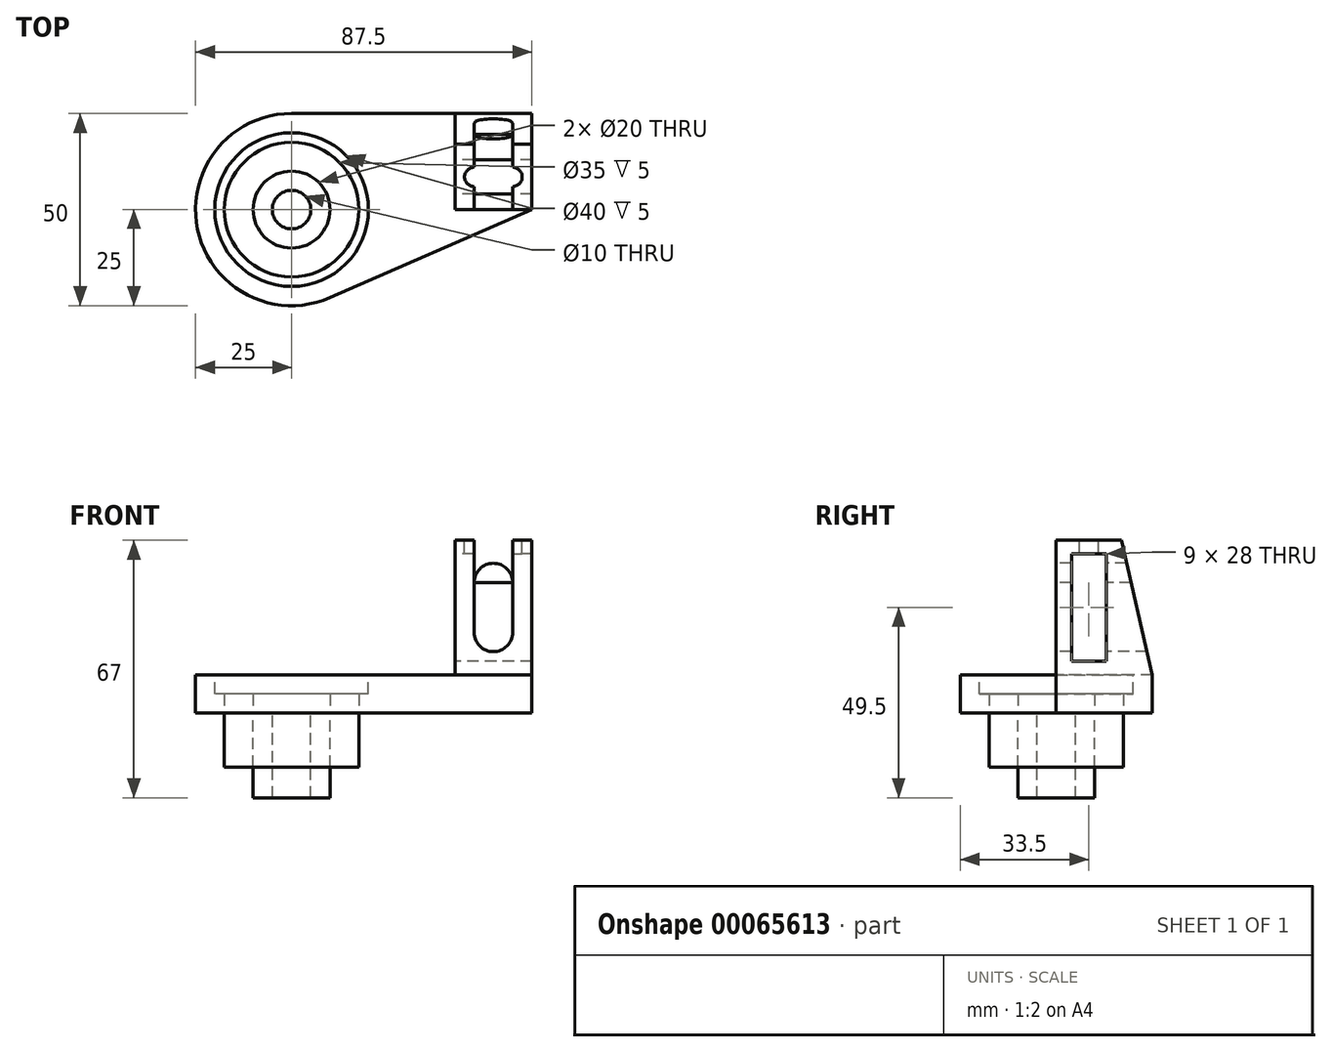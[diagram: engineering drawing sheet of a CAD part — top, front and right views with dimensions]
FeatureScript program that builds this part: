
annotation { "Feature Type Name" : "Feature", "Feature Type Description" : "" }
export const myFeature = defineFeature(function(context is Context, id is Id, definition is map)
    precondition{}
    {
        {
            var Q0;
            Q0=qCreatedBy(makeId("Top.planeOp"),FACE);
            var sketch = newSketch(context, id + "F0", { "sketchPlane" : qUnion([Q0])});
            skCircle(sketch, "E0", {"center": v(0, 0) * mm, "radius": 5 * mm});
            skCircle(sketch, "E1", {"center": v(0, 0) * mm, "radius": 10 * mm});
            skCircle(sketch, "E2", {"center": v(0, 0) * mm, "radius": 17.5 * mm});
            skCircle(sketch, "E3", {"center": v(0, 0) * mm, "radius": 20 * mm});
            skArc(sketch, "E4", {"start": v(0, 25) * mm, "mid": v(-24.47, -5.1) * mm, "end": v(10, -22.91) * mm});
            skLineSegment(sketch, "E5", {"start": v(0, 25) * mm, "end": v(42.5, 25) * mm});
            skLineSegment(sketch, "E6", {"start": v(10, -22.91) * mm, "end": v(62.5, 0) * mm});
            skLineSegment(sketch, "E7", {"start": v(62.5, 0) * mm, "end": v(62.5, 25) * mm});
            skLineSegment(sketch, "E8", {"start": v(62.5, 25) * mm, "end": v(42.5, 25) * mm});
            skLineSegment(sketch, "E9", {"start": v(42.5, 25) * mm, "end": v(42.5, 0) * mm});
            skLineSegment(sketch, "E10", {"start": v(42.5, 0) * mm, "end": v(62.5, 0) * mm});
            skLineSegment(sketch, "E11", {"start": v(62.5, 0) * mm, "end": v(62.5, 17) * mm});
            skLineSegment(sketch, "E12", {"start": v(62.5, 17) * mm, "end": v(42.5, 17) * mm});
            skSolve(sketch);
        }
        {
            var Q0;
            Q0=makeQuery(id+"F0.imprint","IMPRINT",FACE,{"disambiguationData":[TD([[makeQuery(id+"F0.imprint","IMPRINT",EDGE,{"derivedFrom":sQuery(id+"F0.wireOp",EDGE,"E3")}),-1.0]])]});
            var Q1;
            Q1=makeQuery(id+"F0.imprint","IMPRINT",FACE,{"disambiguationData":[TD([[makeQuery(id+"F0.imprint","IMPRINT",EDGE,{"derivedFrom":sQuery(id+"F0.wireOp",EDGE,"E2")}),-1.0]])]});
            extrude(context, id + "F1", {"entities" : qUnion([Q0, Q1]), "depth" : 10 * mm});
        }
        {
            var Q0;
            Q0=makeQuery(id+"F0.imprint","IMPRINT",FACE,{"disambiguationData":[TD([[makeQuery(id+"F0.imprint","IMPRINT",EDGE,{"derivedFrom":sQuery(id+"F0.wireOp",EDGE,"E7")}),1.0]])]});
            var Q1;
            {var subQ0=sQuery(id+"F0.wireOp",EDGE,"E10");Q1=makeQuery(id+"F0.imprint","IMPRINT",FACE,{"disambiguationData":[TD([[makeQuery(id+"F0.imprint","IMPRINT",EDGE,{"derivedFrom":subQ0}),1.0]])]});}
            extrude(context, id + "F2", {"entities" : qUnion([Q0, Q1]), "operationType" : NewBodyOperationType.ADD, "depth" : 45 * mm});
        }
        {
            var Q0;
            Q0=makeQuery(id+"F0.imprint","IMPRINT",FACE,{"disambiguationData":[TD([[makeQuery(id+"F0.imprint","IMPRINT",EDGE,{"derivedFrom":sQuery(id+"F0.wireOp",EDGE,"E0")}),-1.0]])]});
            extrude(context, id + "F3", {"entities" : qUnion([Q0]), "oppositeDirection" : true, "depth" : 22 * mm});
        }
        {
            var Q0;
            Q0=makeQuery(id+"F2.opExtrude","CAP_FACE",FACE,{"disambiguationData":[OSD([sQuery(id+"F0.wireOp",EDGE,"E7"),sQuery(id+"F0.wireOp",EDGE,"E8"),sQuery(id+"F0.wireOp",EDGE,"E9"),sQuery(id+"F0.wireOp",EDGE,"E10"),sQuery(id+"F0.wireOp",EDGE,"E11")])],"isStart":false});
            var sketch = newSketch(context, id + "F4", { "sketchPlane" : qUnion([Q0])});
            skLineSegment(sketch, "E13", {"start": v(62.5, 0) * mm, "end": v(62.5, 17) * mm});
            skLineSegment(sketch, "E14", {"start": v(62.5, 17) * mm, "end": v(42.5, 17) * mm});
            skLineSegment(sketch, "E15", {"start": v(62.5, 0) * mm, "end": v(57.5, 0) * mm});
            skLineSegment(sketch, "E16", {"start": v(57.5, 0) * mm, "end": v(47.5, 0) * mm});
            skLineSegment(sketch, "E17", {"start": v(47.5, 0) * mm, "end": v(42.5, 0) * mm});
            skLineSegment(sketch, "E18", {"start": v(42.5, 0) * mm, "end": v(42.5, 8.5) * mm});
            skLineSegment(sketch, "E19", {"start": v(42.5, 8.5) * mm, "end": v(62.5, 8.5) * mm});
            skLineSegment(sketch, "E20", {"start": v(57.5, 0) * mm, "end": v(57.5, 8.5) * mm});
            skLineSegment(sketch, "E21", {"start": v(47.5, 0) * mm, "end": v(47.5, 8.5) * mm});
            skCircle(sketch, "E22", {"center": v(47.5, 8.5) * mm, "radius": 2.5 * mm});
            skCircle(sketch, "E23", {"center": v(57.5, 8.5) * mm, "radius": 2.5 * mm});
            skSolve(sketch);
        }
        {
            var Q0;
            Q0=makeQuery(id+"F2.opExtrude","CAP_EDGE",EDGE,{"disambiguationData":[OSD([sQuery(id+"F0.wireOp",EDGE,"E8")])],"isStart":false});
            chamfer(context, id + "F5", {"entities" : qUnion([Q0]), "chamferType" : ChamferType.TWO_OFFSETS, "width1" : 8 * mm, "oppositeDirection" : false, "width2" : 35 * mm, "tangentPropagation" : true});
        }
        {
            var Q0;
            Q0=makeQuery(id+"F2.opExtrude","SWEPT_FACE",FACE,{"disambiguationData":[OSD([sQuery(id+"F0.wireOp",EDGE,"E9")])]});
            var sketch = newSketch(context, id + "F6", { "sketchPlane" : qUnion([Q0])});
            skLineSegment(sketch, "E24", {"start": v(0, 10) * mm, "end": v(0, 13.5) * mm});
            skLineSegment(sketch, "E25", {"start": v(0, 45) * mm, "end": v(-4, 45) * mm});
            skLineSegment(sketch, "E26", {"start": v(-4, 45) * mm, "end": v(-13, 45) * mm});
            skLineSegment(sketch, "E27", {"start": v(-13, 45) * mm, "end": v(-17, 45) * mm});
            skLineSegment(sketch, "E28", {"start": v(0, 45) * mm, "end": v(0, 41.5) * mm});
            skLineSegment(sketch, "E29", {"start": v(0, 41.5) * mm, "end": v(-17.8, 41.5) * mm});
            skLineSegment(sketch, "E30", {"start": v(-4, 45) * mm, "end": v(-4, 10) * mm});
            skLineSegment(sketch, "E31", {"start": v(0, 13.5) * mm, "end": v(-24.2, 13.5) * mm});
            skLineSegment(sketch, "E32", {"start": v(-13, 45) * mm, "end": v(-13, 10) * mm});
            skPoint(sketch, "E33", {"position": v(-13, 41.5) * mm});
            skPoint(sketch, "E34", {"position": v(-4, 41.5) * mm});
            skPoint(sketch, "E35", {"position": v(-4, 13.5) * mm});
            skPoint(sketch, "E36", {"position": v(-13, 13.5) * mm});
            skSolve(sketch);
        }
        {
            var Q0;
            {var subQ0=sQuery(id+"F6.wireOp",EDGE,"E30");var subQ1=sQuery(id+"F6.wireOp",EDGE,"E29");var subQ2=makeQuery(id+"F6.imprint","INTERSECT",VERTEX,{"derivedFrom":[subQ1,subQ0]});Q0=makeQuery(id+"F6.imprint","IMPRINT",FACE,{"disambiguationData":[TD([[makeQuery(id+"F6.imprint","IMPRINT",EDGE,{"disambiguationData":[TD([[subQ2,-1.0]])],"derivedFrom":subQ1}),1.0]])]});}
            extrude(context, id + "F7", {"entities" : qUnion([Q0]), "operationType" : NewBodyOperationType.REMOVE, "oppositeDirection" : true, "depth" : 30 * mm});
        }
        {
            var Q0;
            Q0=makeQuery(id+"F2.opExtrude","SWEPT_FACE",FACE,{"disambiguationData":[OSD([sQuery(id+"F0.wireOp",EDGE,"E10")])]});
            var sketch = newSketch(context, id + "F8", { "sketchPlane" : qUnion([Q0])});
            skLineSegment(sketch, "E37", {"start": v(62.5, 45) * mm, "end": v(62.5, 34) * mm});
            skLineSegment(sketch, "E38", {"start": v(62.5, 34) * mm, "end": v(62.5, 21) * mm});
            skLineSegment(sketch, "E39", {"start": v(42.5, 45) * mm, "end": v(47.5, 45) * mm});
            skLineSegment(sketch, "E40", {"start": v(47.5, 45) * mm, "end": v(57.5, 45) * mm});
            skLineSegment(sketch, "E41", {"start": v(57.5, 45) * mm, "end": v(62.5, 45) * mm});
            skLineSegment(sketch, "E42", {"start": v(57.5, 45) * mm, "end": v(57.5, 10) * mm});
            skLineSegment(sketch, "E43", {"start": v(47.5, 45) * mm, "end": v(47.5, 10) * mm});
            skLineSegment(sketch, "E44", {"start": v(62.5, 21) * mm, "end": v(42.5, 21) * mm});
            skLineSegment(sketch, "E45", {"start": v(62.5, 34) * mm, "end": v(42.5, 34) * mm});
            skArc(sketch, "E46", {"start": v(47.5, 34) * mm, "mid": v(52.5, 39) * mm, "end": v(57.5, 34) * mm});
            skArc(sketch, "E47", {"start": v(47.5, 21) * mm, "mid": v(52.5, 16) * mm, "end": v(57.5, 21) * mm});
            skPoint(sketch, "E47.startSnap0", {"position": v(52.5, 21) * mm});
            skSolve(sketch);
        }
        {
            var Q0;
            {var subQ0=sQuery(id+"F8.wireOp",EDGE,"E46");Q0=makeQuery(id+"F8.imprint","IMPRINT",FACE,{"disambiguationData":[TD([[makeQuery(id+"F8.imprint","IMPRINT",EDGE,{"derivedFrom":subQ0}),-1.0]])]});}
            var Q1;
            {var subQ0=sQuery(id+"F8.wireOp",EDGE,"E46");var subQ1=sQuery(id+"F8.wireOp",EDGE,"E45");var subQ2=sQuery(id+"F8.wireOp",EDGE,"E42");var subQ3=makeQuery(id+"F8.imprint","INTERSECT",VERTEX,{"derivedFrom":[subQ2,subQ1,subQ0]});Q1=makeQuery(id+"F8.imprint","IMPRINT",FACE,{"disambiguationData":[TD([[makeQuery(id+"F8.imprint","IMPRINT",EDGE,{"disambiguationData":[TD([[subQ3,-1.0]])],"derivedFrom":subQ2}),-1.0]])]});}
            var Q2;
            {var subQ0=sQuery(id+"F8.wireOp",EDGE,"E47");Q2=makeQuery(id+"F8.imprint","IMPRINT",FACE,{"disambiguationData":[TD([[makeQuery(id+"F8.imprint","IMPRINT",EDGE,{"derivedFrom":subQ0}),1.0]])]});}
            extrude(context, id + "F9", {"entities" : qUnion([Q0, Q1, Q2]), "operationType" : NewBodyOperationType.REMOVE, "oppositeDirection" : true, "depth" : 26 * mm});
        }
        {
            var Q0;
            {var subQ0=sQuery(id+"F4.wireOp",EDGE,"E19");var subQ1=makeQuery(id+"F4.imprint","INTERSECT",VERTEX,{"derivedFrom":[subQ0,sQuery(id+"F4.wireOp",EDGE,"E21")]});Q0=makeQuery(id+"F4.imprint","IMPRINT",FACE,{"disambiguationData":[TD([[makeQuery(id+"F4.imprint","IMPRINT",EDGE,{"disambiguationData":[TD([[subQ1,1.0]])],"derivedFrom":subQ0}),1.0]])]});}
            var Q1;
            {var subQ0=sQuery(id+"F4.wireOp",EDGE,"E21");var subQ1=sQuery(id+"F4.wireOp",EDGE,"E19");var subQ2=makeQuery(id+"F4.imprint","INTERSECT",VERTEX,{"derivedFrom":[subQ1,subQ0]});Q1=makeQuery(id+"F4.imprint","IMPRINT",FACE,{"disambiguationData":[TD([[makeQuery(id+"F4.imprint","IMPRINT",EDGE,{"disambiguationData":[TD([[subQ2,1.0]])],"derivedFrom":subQ1}),-1.0]])]});}
            var Q2;
            {var subQ0=sQuery(id+"F4.wireOp",EDGE,"E21");var subQ1=sQuery(id+"F4.wireOp",EDGE,"E19");var subQ2=makeQuery(id+"F4.imprint","INTERSECT",VERTEX,{"derivedFrom":[subQ1,subQ0]});Q2=makeQuery(id+"F4.imprint","IMPRINT",FACE,{"disambiguationData":[TD([[makeQuery(id+"F4.imprint","IMPRINT",EDGE,{"disambiguationData":[TD([[subQ2,-1.0]])],"derivedFrom":subQ1}),-1.0]])]});}
            var Q3;
            {var subQ0=sQuery(id+"F4.wireOp",EDGE,"E19");var subQ1=makeQuery(id+"F4.imprint","INTERSECT",VERTEX,{"derivedFrom":[subQ0,sQuery(id+"F4.wireOp",EDGE,"E20")]});Q3=makeQuery(id+"F4.imprint","IMPRINT",FACE,{"disambiguationData":[TD([[makeQuery(id+"F4.imprint","IMPRINT",EDGE,{"disambiguationData":[TD([[subQ1,1.0]])],"derivedFrom":subQ0}),1.0]])]});}
            var Q4;
            {var subQ0=sQuery(id+"F4.wireOp",EDGE,"E20");var subQ1=sQuery(id+"F4.wireOp",EDGE,"E19");var subQ2=makeQuery(id+"F4.imprint","INTERSECT",VERTEX,{"derivedFrom":[subQ1,subQ0]});Q4=makeQuery(id+"F4.imprint","IMPRINT",FACE,{"disambiguationData":[TD([[makeQuery(id+"F4.imprint","IMPRINT",EDGE,{"disambiguationData":[TD([[subQ2,1.0]])],"derivedFrom":subQ1}),-1.0]])]});}
            var Q5;
            {var subQ0=sQuery(id+"F4.wireOp",EDGE,"E20");var subQ1=sQuery(id+"F4.wireOp",EDGE,"E19");var subQ2=makeQuery(id+"F4.imprint","INTERSECT",VERTEX,{"derivedFrom":[subQ1,subQ0]});Q5=makeQuery(id+"F4.imprint","IMPRINT",FACE,{"disambiguationData":[TD([[makeQuery(id+"F4.imprint","IMPRINT",EDGE,{"disambiguationData":[TD([[subQ2,-1.0]])],"derivedFrom":subQ1}),-1.0]])]});}
            extrude(context, id + "F10", {"entities" : qUnion([Q0, Q1, Q2, Q3, Q4, Q5]), "operationType" : NewBodyOperationType.REMOVE, "oppositeDirection" : true, "depth" : 25 * mm});
        }
        {
            var Q0;
            Q0=makeQuery(id+"F1.opExtrude","CAP_FACE",FACE,{"disambiguationData":[OSD([sQuery(id+"F0.wireOp",EDGE,"E2"),sQuery(id+"F0.wireOp",EDGE,"E4"),sQuery(id+"F0.wireOp",EDGE,"E5"),sQuery(id+"F0.wireOp",EDGE,"E6"),sQuery(id+"F0.wireOp",EDGE,"E9"),sQuery(id+"F0.wireOp",EDGE,"E10")])],"isStart":false});
            var sketch = newSketch(context, id + "F11", { "sketchPlane" : qUnion([Q0])});
            skCircle(sketch, "E48", {"center": v(0, 0) * mm, "radius": 20 * mm});
            skSolve(sketch);
        }
        {
            var Q0;
            Q0=makeQuery(id+"F11.imprint","IMPRINT",FACE,{"disambiguationData":[TD([[makeQuery(id+"F11.imprint","IMPRINT",EDGE,{"derivedFrom":sQuery(id+"F11.wireOp",EDGE,"E48")}),1.0]])]});
            extrude(context, id + "F12", {"entities" : qUnion([Q0]), "operationType" : NewBodyOperationType.REMOVE, "oppositeDirection" : true, "depth" : 5 * mm});
        }
        {
            var Q0;
            Q0=makeQuery(id+"F0.imprint","IMPRINT",FACE,{"disambiguationData":[TD([[makeQuery(id+"F0.imprint","IMPRINT",EDGE,{"derivedFrom":sQuery(id+"F0.wireOp",EDGE,"E1")}),-1.0]])]});
            extrude(context, id + "F13", {"entities" : qUnion([Q0]), "oppositeDirection" : true, "depth" : 14 * mm});
        }
        {
            var Q0;
            Q0=makeQuery(id+"F0.imprint","IMPRINT",FACE,{"disambiguationData":[TD([[makeQuery(id+"F0.imprint","IMPRINT",EDGE,{"derivedFrom":sQuery(id+"F0.wireOp",EDGE,"E1")}),-1.0]])]});
            extrude(context, id + "F14", {"entities" : qUnion([Q0]), "depth" : 5 * mm});
        }
    });
